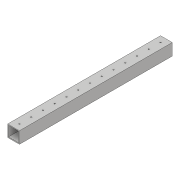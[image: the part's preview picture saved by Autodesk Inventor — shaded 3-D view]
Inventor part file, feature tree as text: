
AUTODESK INVENTOR PART (.ipt)
format: ipt  version: 2018 (Build 220112000, 112)  size: 113,152 bytes
history: native  units: in
note: dims shown in document units (in); Inventor stores cm internally (conversion verified against a paired STEP export)
features: sketch x2, extrude x1, hole x1
ambient origin geometry x8: Origin, YZ Plane, XZ Plane, XY Plane, X Axis, Y Axis, Z Axis, Center Point
bodies: Solid1 (feature_tree)
feature tree (4):
  extrude  "Extrusion1"  Depth=1.0in
  hole  "Hole1"  [1 undecoded]
  sketch  "Sketch1"  dims[d0=1.0in d1=1.0in]
  sketch  "Sketch2"  dims[d2=0.0625in d3=0.0625in d4=13.0in d5=0.0in d6=0.5in d7=0.5in d8=5.9055in d10=1.0in d11=0.3937in d13=1.0in d15=0.1in d16=0.75in d17=0.375in d18=0.25in d19=0.5635in d20=1.0in d21=0.8108in]
note: 1 required parameter value undecoded (feature->parameter linkage not recoverable at this tier; creation-order binding heuristic only, values carry confidence <= 0.55)
